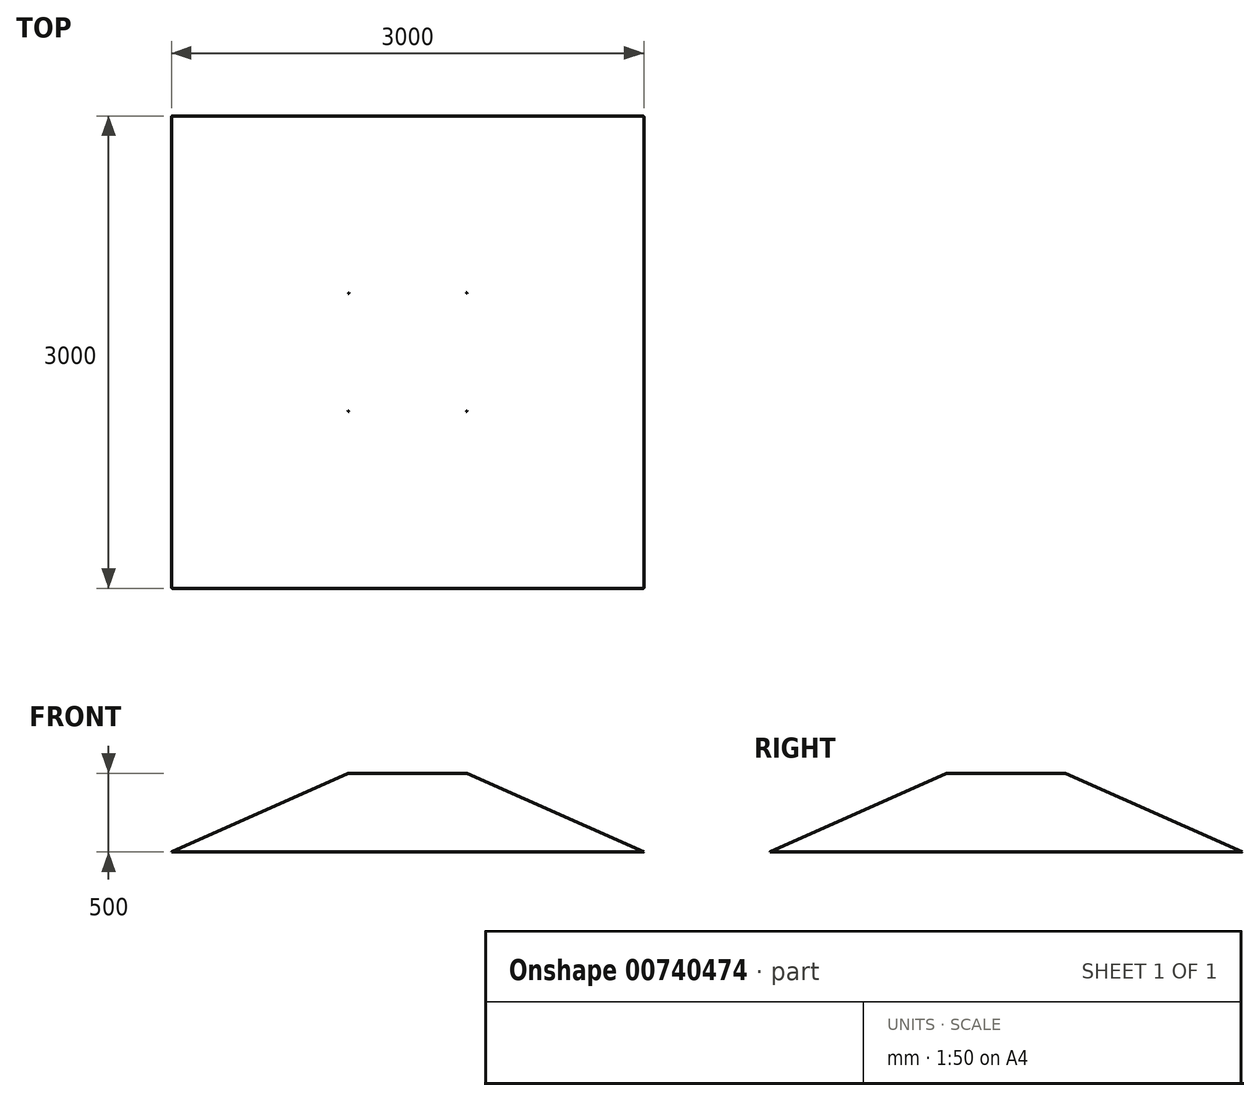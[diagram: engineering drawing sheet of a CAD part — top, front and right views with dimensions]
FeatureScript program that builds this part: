
annotation { "Feature Type Name" : "Feature", "Feature Type Description" : "" }
export const myFeature = defineFeature(function(context is Context, id is Id, definition is map)
    precondition{}
    {
        {
            var Q0;
            Q0=qCreatedBy(makeId("Top.planeOp"),FACE);
            var sketch = newSketch(context, id + "F0", { "sketchPlane" : qUnion([Q0])});
            skLineSegment(sketch, "E0.bottom", {"start": v(1500, 1500) * mm, "end": v(-1500, 1500) * mm});
            skLineSegment(sketch, "E0.top", {"start": v(1500, -1500) * mm, "end": v(-1500, -1500) * mm});
            skLineSegment(sketch, "E0.left", {"start": v(1500, 1500) * mm, "end": v(1500, -1500) * mm});
            skLineSegment(sketch, "E0.right", {"start": v(-1500, 1500) * mm, "end": v(-1500, -1500) * mm});
            skSolve(sketch);
        }
        {
            var Q0;
            Q0=makeQuery(id+"F0.imprint","IMPRINT",FACE,{"disambiguationData":[TD([[makeQuery(id+"F0.imprint","IMPRINT",EDGE,{"derivedFrom":sQuery(id+"F0.wireOp",EDGE,"E0.bottom")}),1.0]])]});
            cPlane(context, id + "F1", {"entities" : qUnion([Q0]), "cplaneType" : CPlaneType.OFFSET, "offset" : 500 * mm, "width" : 150 * mm, "height" : 150 * mm});
        }
        {
            var Q0;
            Q0=qCreatedBy(id+"F1.planeOp",FACE);
            var sketch = newSketch(context, id + "F2", { "sketchPlane" : qUnion([Q0])});
            skLineSegment(sketch, "E1.bottom", {"start": v(-375, 375) * mm, "end": v(375, 375) * mm});
            skLineSegment(sketch, "E1.top", {"start": v(-375, -375) * mm, "end": v(375, -375) * mm});
            skLineSegment(sketch, "E1.left", {"start": v(-375, 375) * mm, "end": v(-375, -375) * mm});
            skLineSegment(sketch, "E1.right", {"start": v(375, 375) * mm, "end": v(375, -375) * mm});
            skPoint(sketch, "E1.middle", {"position": v(0, 0) * mm});
            skSolve(sketch);
        }
        {
            var Q0;
            Q0 = qSketchRegion(id + "F0", true);
            var Q1;
            Q1 = qSketchRegion(id + "F2", true);
            loft(context, id + "F3", {"sheetProfilesArray" : [{ "sheetProfileEntities" : qUnion([Q0]) }, { "sheetProfileEntities" : qUnion([Q1]) }]});
        }
        {
            var Q0;
            Q0=makeQuery(id+"F3.opLoft","SWEPT_EDGE",EDGE,{"disambiguationData":[OSD([sQuery(id+"F0.wireOp",EDGE,"E0.bottom"),sQuery(id+"F0.wireOp",EDGE,"E0.right"),sQuery(id+"F2.wireOp",EDGE,"E1.bottom"),sQuery(id+"F2.wireOp",EDGE,"E1.left")])]});
            var Q1;
            Q1=makeQuery(id+"F3.opLoft","CAP_FACE",FACE,{"disambiguationData":[OSD([makeQuery(id+"F2.imprint","IMPRINT",FACE,{"disambiguationData":[TD([[makeQuery(id+"F2.imprint","IMPRINT",EDGE,{"derivedFrom":sQuery(id+"F2.wireOp",EDGE,"E1.bottom")}),-1.0]])]})])],"isStart":true});
            var Q2;
            Q2=makeQuery(id+"F3.opLoft","SWEPT_EDGE",EDGE,{"disambiguationData":[OSD([sQuery(id+"F0.wireOp",EDGE,"E0.top"),sQuery(id+"F0.wireOp",EDGE,"E0.right"),sQuery(id+"F2.wireOp",EDGE,"E1.top"),sQuery(id+"F2.wireOp",EDGE,"E1.left")])]});
            var Q3;
            Q3=makeQuery(id+"F3.opLoft","SWEPT_EDGE",EDGE,{"disambiguationData":[OSD([sQuery(id+"F0.wireOp",EDGE,"E0.top"),sQuery(id+"F0.wireOp",EDGE,"E0.left"),sQuery(id+"F2.wireOp",EDGE,"E1.top"),sQuery(id+"F2.wireOp",EDGE,"E1.right")])]});
            var Q4;
            Q4=makeQuery(id+"F3.opLoft","SWEPT_EDGE",EDGE,{"disambiguationData":[OSD([sQuery(id+"F0.wireOp",EDGE,"E0.bottom"),sQuery(id+"F0.wireOp",EDGE,"E0.left"),sQuery(id+"F2.wireOp",EDGE,"E1.bottom"),sQuery(id+"F2.wireOp",EDGE,"E1.right")])]});
            fillet(context, id + "F4", {"entities" : qUnion([Q0, Q1, Q2, Q3, Q4]), "radius" : 13 * mm, "tangentPropagation" : true, "allowEdgeOverflow" : false});
        }
    });
